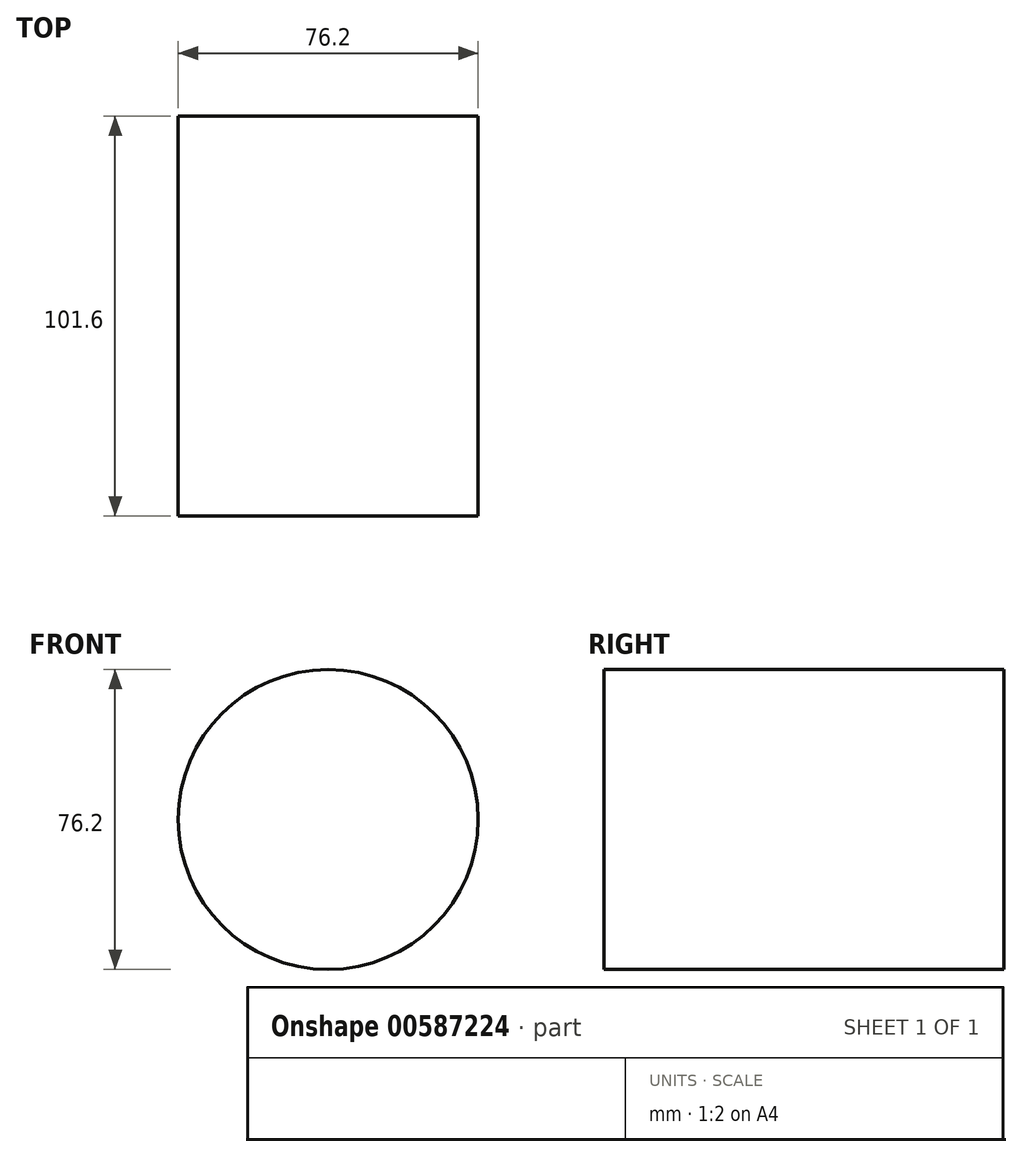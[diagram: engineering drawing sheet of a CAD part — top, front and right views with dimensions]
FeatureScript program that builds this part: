
annotation { "Feature Type Name" : "Feature", "Feature Type Description" : "" }
export const myFeature = defineFeature(function(context is Context, id is Id, definition is map)
    precondition{}
    {
        {
            var Q0;
            Q0=qCreatedBy(makeId("Front.planeOp"),FACE);
            var sketch = newSketch(context, id + "F0", { "sketchPlane" : qUnion([Q0])});
            skCircle(sketch, "E0", {"center": v(0, 0) * mm, "radius": 38.1 * mm});
            skSolve(sketch);
        }
        {
            var Q0;
            Q0=makeQuery(id+"F0.imprint","IMPRINT",FACE,{"disambiguationData":[TD([[makeQuery(id+"F0.imprint","IMPRINT",EDGE,{"derivedFrom":sQuery(id+"F0.wireOp",EDGE,"E0")}),1.0]])]});
            extrude(context, id + "F1", {"entities" : qUnion([Q0]), "depth" : 101.6 * mm, "offsetDistance" : 25.4 * mm});
        }
    });
